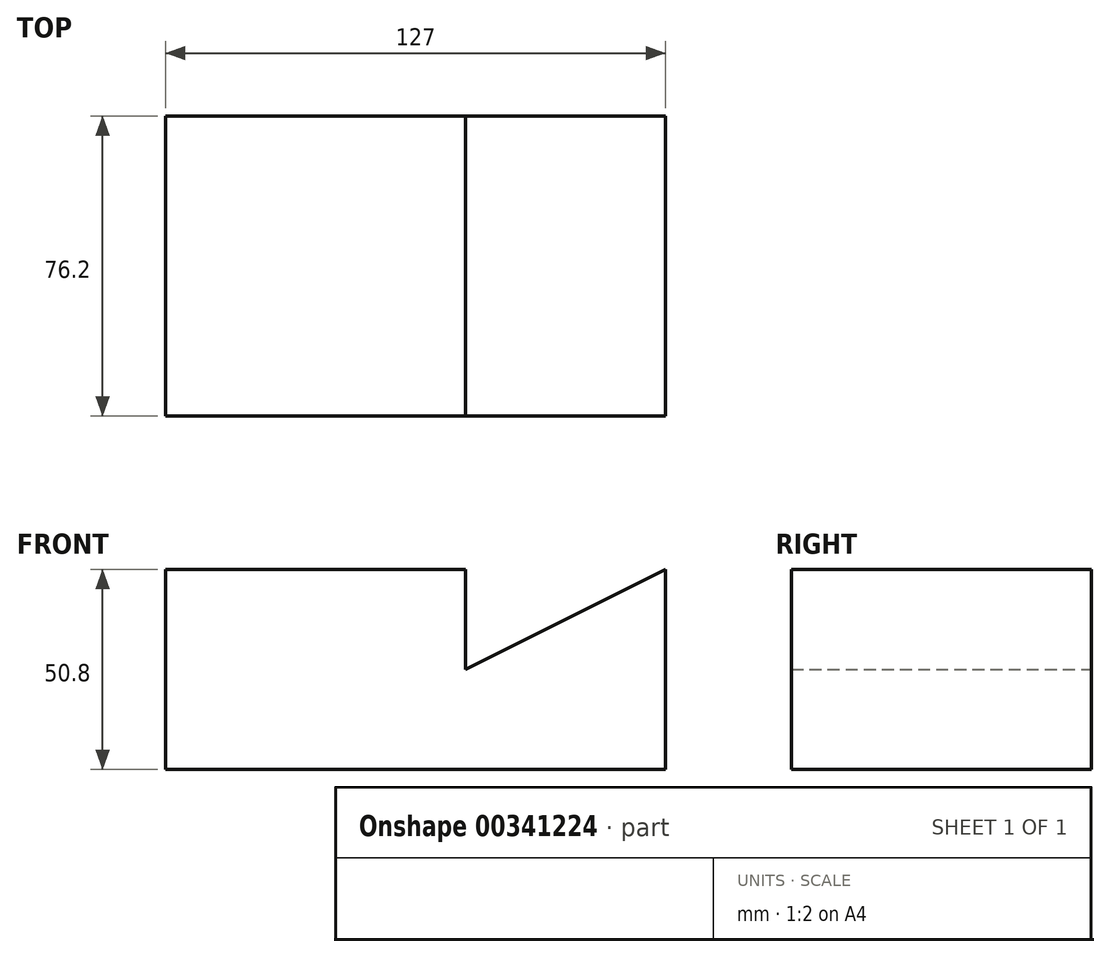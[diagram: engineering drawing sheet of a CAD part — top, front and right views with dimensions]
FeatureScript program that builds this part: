
annotation { "Feature Type Name" : "Feature", "Feature Type Description" : "" }
export const myFeature = defineFeature(function(context is Context, id is Id, definition is map)
    precondition{}
    {
        {
            var Q0;
            Q0=qCreatedBy(makeId("Front.planeOp"),FACE);
            var sketch = newSketch(context, id + "F0", { "sketchPlane" : qUnion([Q0])});
            skLineSegment(sketch, "E0", {"start": v(0, 0) * mm, "end": v(0, 50.8) * mm});
            skLineSegment(sketch, "E1", {"start": v(0, 50.8) * mm, "end": v(76.2, 50.8) * mm});
            skLineSegment(sketch, "E2", {"start": v(76.2, 50.8) * mm, "end": v(76.2, 25.4) * mm});
            skLineSegment(sketch, "E3", {"start": v(76.2, 25.4) * mm, "end": v(127, 50.8) * mm});
            skLineSegment(sketch, "E4", {"start": v(127, 50.8) * mm, "end": v(127, 0) * mm});
            skLineSegment(sketch, "E5", {"start": v(127, 0) * mm, "end": v(0, 0) * mm});
            skSolve(sketch);
        }
        {
            var Q0;
            Q0 = qSketchRegion(id + "F0", true);
            extrude(context, id + "F1", {"entities" : qUnion([Q0]), "depth" : 76.2 * mm});
        }
    });
